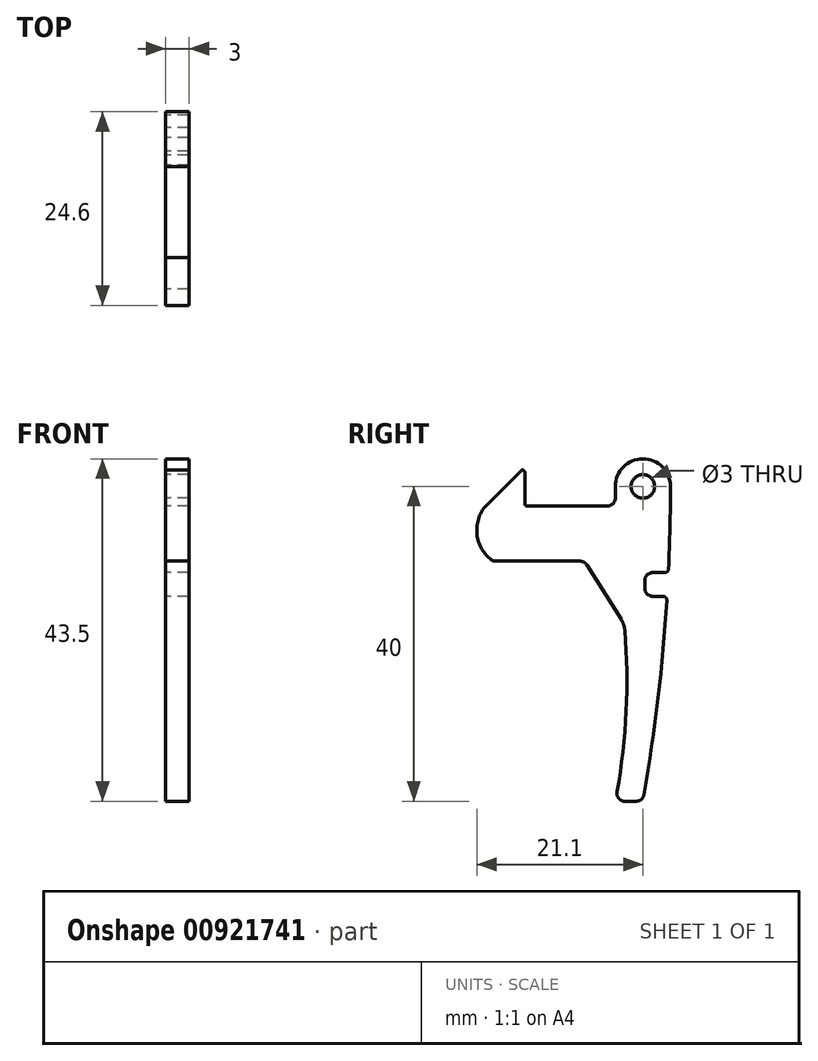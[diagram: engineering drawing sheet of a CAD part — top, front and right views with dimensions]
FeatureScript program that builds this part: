
annotation { "Feature Type Name" : "Feature", "Feature Type Description" : "" }
export const myFeature = defineFeature(function(context is Context, id is Id, definition is map)
    precondition{}
    {
        {
            var Q0;
            Q0=qCreatedBy(makeId("Right.planeOp"),FACE);
            var sketch = newSketch(context, id + "F0", { "sketchPlane" : qUnion([Q0])});
            skCircle(sketch, "E0", {"center": v(0, 0) * mm, "radius": 1.5 * mm});
            skArc(sketch, "E1", {"start": v(3.5, 0) * mm, "mid": v(0, 3.5) * mm, "end": v(-3.5, 0) * mm});
            skLineSegment(sketch, "E2", {"start": v(0, 0) * mm, "end": v(0, -2.5) * mm});
            skLineSegment(sketch, "E3", {"start": v(-4.5, -2.5) * mm, "end": v(-14.7, -2.5) * mm});
            skLineSegment(sketch, "E4", {"start": v(-15, 1.78) * mm, "end": v(-15, -2.2) * mm});
            skLineSegment(sketch, "E5", {"start": v(-19, -9.5) * mm, "end": v(-7.97, -9.5) * mm});
            skLineSegment(sketch, "E6", {"start": v(-15.51, 1.99) * mm, "end": v(-19.7, -2.2) * mm});
            skLineSegment(sketch, "E7", {"start": v(-3.5, 0) * mm, "end": v(-3.5, -1.5) * mm});
            skLineSegment(sketch, "E8", {"start": v(-2.3, -40) * mm, "end": v(-0.84, -40) * mm});
            skPoint(sketch, "E9.orphan", {"position": v(0, -9.5) * mm});
            skArc(sketch, "E10", {"start": v(0.14, -39.17) * mm, "mid": v(1.93, -26.87) * mm, "end": v(3.04, -14.5) * mm});
            skArc(sketch, "E11", {"start": v(-3.28, -38.82) * mm, "mid": v(-2.13, -28.58) * mm, "end": v(-2.3, -18.27) * mm});
            skPoint(sketch, "E12.visualSharp", {"position": v(-3.5, -40) * mm});
            skArc(sketch, "E12.filletArc", {"start": v(-3.28, -38.82) * mm, "mid": v(-3.06, -39.64) * mm, "end": v(-2.3, -40) * mm});
            skPoint(sketch, "E13.newPointA", {"position": v(0, -40) * mm});
            skPoint(sketch, "E13.newPointB", {"position": v(3.5, -40) * mm});
            skArc(sketch, "E13.filletArc", {"start": v(-0.84, -40) * mm, "mid": v(-0.2, -39.76) * mm, "end": v(0.14, -39.17) * mm});
            skPoint(sketch, "E14.visualSharp", {"position": v(-20, -2.5) * mm});
            skPoint(sketch, "E15.visualSharp", {"position": v(-20, -9.5) * mm});
            skPoint(sketch, "E16.visualSharp", {"position": v(-3.5, -9.5) * mm});
            skPoint(sketch, "E17.visualSharp", {"position": v(-3.5, -2.5) * mm});
            skArc(sketch, "E17.filletArc", {"start": v(-4.5, -2.5) * mm, "mid": v(-3.8, -2.2) * mm, "end": v(-3.5, -1.5) * mm});
            skPoint(sketch, "E18.visualSharp", {"position": v(-15, 2.5) * mm});
            skArc(sketch, "E18.filletArc", {"start": v(-15, 1.78) * mm, "mid": v(-15.19, 2.05) * mm, "end": v(-15.51, 1.99) * mm});
            skPoint(sketch, "E19.visualSharp", {"position": v(-15, -2.5) * mm});
            skArc(sketch, "E19.filletArc", {"start": v(-15, -2.2) * mm, "mid": v(-14.91, -2.41) * mm, "end": v(-14.7, -2.5) * mm});
            skArc(sketch, "E20", {"start": v(-19.7, -2.2) * mm, "mid": v(-21.07, -6.02) * mm, "end": v(-19, -9.5) * mm});
            skLineSegment(sketch, "E21", {"start": v(-7.12, -9.97) * mm, "end": v(-2.75, -16.92) * mm});
            skLineSegment(sketch, "E22.bottom", {"start": v(2.76, -10.96) * mm, "end": v(1.24, -10.96) * mm});
            skLineSegment(sketch, "E22.top", {"start": v(2.54, -13.96) * mm, "end": v(1.24, -13.96) * mm});
            skLineSegment(sketch, "E22.right", {"start": v(0.24, -11.96) * mm, "end": v(0.24, -12.96) * mm});
            skArc(sketch, "E23.trimOffspring", {"start": v(3.26, -10.48) * mm, "mid": v(3.44, -5.24) * mm, "end": v(3.5, 0) * mm});
            skPoint(sketch, "E24.visualSharp", {"position": v(0.24, -10.96) * mm});
            skArc(sketch, "E24.filletArc", {"start": v(1.24, -10.96) * mm, "mid": v(0.53, -11.25) * mm, "end": v(0.24, -11.96) * mm});
            skPoint(sketch, "E25.visualSharp", {"position": v(0.24, -13.96) * mm});
            skArc(sketch, "E25.filletArc", {"start": v(0.24, -12.96) * mm, "mid": v(0.53, -13.67) * mm, "end": v(1.24, -13.96) * mm});
            skPoint(sketch, "E26.visualSharp", {"position": v(3.24, -10.96) * mm});
            skArc(sketch, "E26.filletArc", {"start": v(2.76, -10.96) * mm, "mid": v(3.1, -10.82) * mm, "end": v(3.26, -10.48) * mm});
            skArc(sketch, "E27.filletArc", {"start": v(3.04, -14.5) * mm, "mid": v(2.9, -14.12) * mm, "end": v(2.54, -13.96) * mm});
            skPoint(sketch, "E28.visualSharp", {"position": v(-2.36, -17.53) * mm});
            skArc(sketch, "E28.filletArc", {"start": v(-2.3, -18.27) * mm, "mid": v(-2.44, -17.57) * mm, "end": v(-2.75, -16.92) * mm});
            skPoint(sketch, "E29.visualSharp", {"position": v(-7.42, -9.5) * mm});
            skArc(sketch, "E29.filletArc", {"start": v(-7.12, -9.97) * mm, "mid": v(-7.49, -9.62) * mm, "end": v(-7.97, -9.5) * mm});
            skSolve(sketch);
        }
        {
            var Q0;
            Q0 = qSketchRegion(id + "F0", true);
            extrude(context, id + "F1", {"entities" : qUnion([Q0]), "depth" : 3 * mm, "offsetDistance" : 25 * mm});
        }
    });
